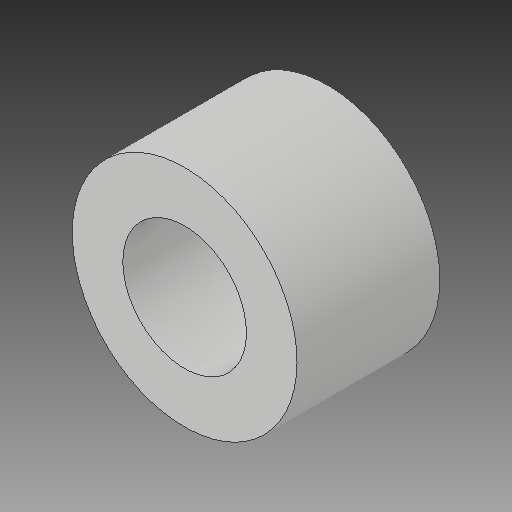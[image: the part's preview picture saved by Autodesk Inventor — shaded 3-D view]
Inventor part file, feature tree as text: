
AUTODESK INVENTOR PART (.ipt)
format: ipt  version: 2017 (Build 210142000, 142)  size: 100,864 bytes
history: native  units: mm
features: other x3, sketch x1
ambient origin geometry x8: Origin, YZ Plane, XZ Plane, XY Plane, X Axis, Y Axis, Z Axis, Center Point
bodies: Solid1 (feature_tree)
feature tree (4):
  other  "Small-Aluminium-Spacer_MIR.ipt"
  other  "Solid1::Small-Aluminium-Spacer_MIR.ipt"
  other  "TaggingFeature1"
  sketch  "Sketch1"  dims[d0=10.0mm]
